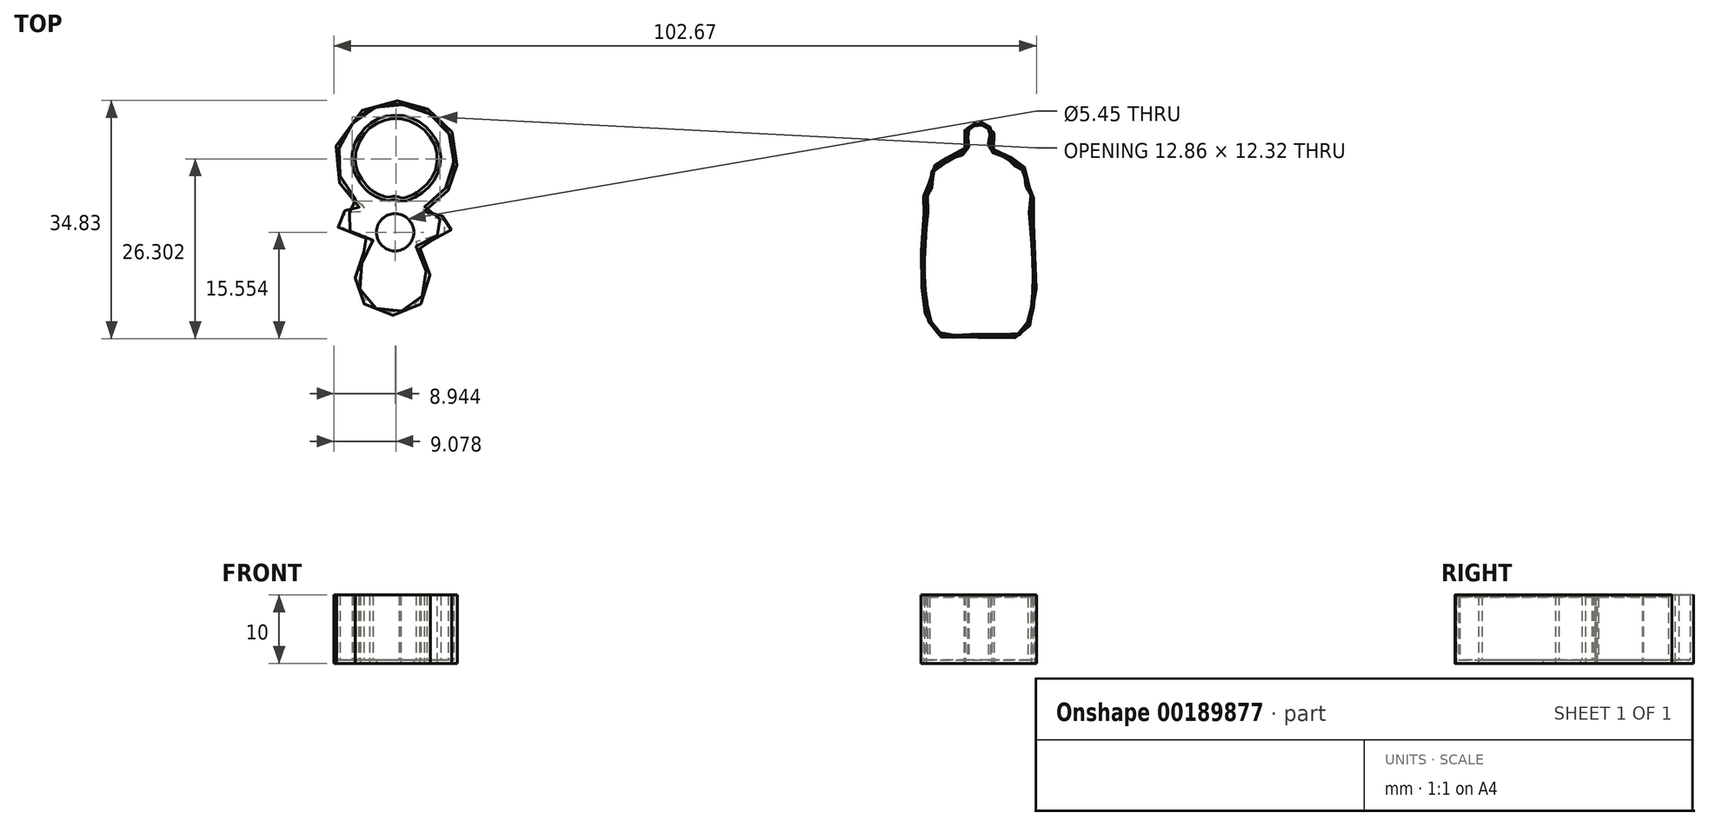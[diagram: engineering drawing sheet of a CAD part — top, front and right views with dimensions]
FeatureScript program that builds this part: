
annotation { "Feature Type Name" : "Feature", "Feature Type Description" : "" }
export const myFeature = defineFeature(function(context is Context, id is Id, definition is map)
    precondition{}
    {
        {
            var Q0;
            Q0=qCreatedBy(makeId("Top.planeOp"),FACE);
            var sketch = newSketch(context, id + "F0", { "sketchPlane" : qUnion([Q0])});
            skFitSpline(sketch, "E0", {"points": [v(-48.43, 29.19) * mm, v(-45.9, 31.2) * mm, v(-44.38, 33.3) * mm, v(-43.72, 35.4) * mm, v(-43.8, 39.13) * mm, v(-45.02, 41.74) * mm, v(-47.94, 44.21) * mm, v(-50.92, 45.2) * mm, v(-54.18, 45.32) * mm, v(-58.63, 43.06) * mm, v(-61.53, 37.77) * mm, v(-60.92, 33.6) * mm, v(-58.75, 30.52) * mm, v(-57.75, 29.7) * mm, v(-57.73, 29.65) * mm, v(-58.6, 29.62) * mm, v(-60.27, 29.17) * mm, v(-61.16, 28.22) * mm, v(-61.13, 27.06) * mm, v(-59.43, 25.82) * mm, v(-56.55, 25.26) * mm, v(-56.44, 25.26) * mm, v(-56.5, 24.8) * mm, v(-57.3, 23.15) * mm, v(-58.25, 21.18) * mm, v(-58.46, 18.34) * mm, v(-57.63, 16.15) * mm, v(-55.65, 14.53) * mm, v(-52.2, 14.04) * mm, v(-49.52, 15.11) * mm, v(-47.93, 17.32) * mm, v(-47.7, 20.56) * mm, v(-48.96, 23.46) * mm, v(-49.08, 23.89) * mm, v(-49.1, 24.68) * mm, v(-49, 24.74) * mm, v(-46.78, 25.09) * mm, v(-44.95, 25.77) * mm, v(-44.5, 26.48) * mm, v(-44.52, 27.45) * mm, v(-45.1, 28.21) * mm, v(-46.6, 28.74) * mm, v(-48.11, 29.1) * mm, v(-48.4, 29.14) * mm, v(-48.43, 29.19) * mm]});
            skFitSpline(sketch, "E1", {"points": [v(-51.83, 31.14) * mm, v(-50.03, 31.7) * mm, v(-49.62, 31.9) * mm, v(-47.4, 34) * mm, v(-46.84, 38.74) * mm, v(-50.67, 42.47) * mm, v(-55.22, 42.15) * mm, v(-58.4, 37.99) * mm], "startDerivative": vector(5.8, -4.1) * mm, "endDerivative": vector(-10.4, -36.58) * mm});
            skFitSpline(sketch, "E2", {"points": [v(-58.4, 37.99) * mm, v(-58.49, 37.04) * mm, v(-58.2, 35.19) * mm, v(-56.71, 32.82) * mm, v(-55.36, 31.86) * mm, v(-53.73, 31.29) * mm, v(-52.96, 31.42) * mm, v(-52.17, 31.34) * mm, v(-51.83, 31.14) * mm], "startDerivative": vector(-1.02, -8.1) * mm, "endDerivative": vector(4.18, -3.1) * mm});
            skSolve(sketch);
        }
        {
            var Q0;
            Q0 = qSketchRegion(id + "F0", true);
            extrude(context, id + "F1", {"entities" : qUnion([Q0]), "depth" : 10 * mm});
        }
        {
            var Q0;
            Q0=makeQuery(id+"F1.opExtrude","CAP_FACE",FACE,{"disambiguationData":[OSD([sQuery(id+"F0.wireOp",EDGE,"E0"),sQuery(id+"F0.wireOp",EDGE,"E1"),sQuery(id+"F0.wireOp",EDGE,"E2")])],"isStart":false});
            shell(context, id + "F2", {"entities" : qUnion([Q0]), "thickness" : .5 * mm});
        }
        {
            var Q0;
            Q0=makeQuery(id+"F1.opExtrude","CAP_FACE",FACE,{"disambiguationData":[OSD([sQuery(id+"F0.wireOp",EDGE,"E0"),sQuery(id+"F0.wireOp",EDGE,"E1"),sQuery(id+"F0.wireOp",EDGE,"E2")])],"isStart":true});
            var sketch = newSketch(context, id + "F3", { "sketchPlane" : qUnion([Q0])});
            skCircle(sketch, "E3", {"center": v(-52.69, -26.14) * mm, "radius": 2.73 * mm});
            skSolve(sketch);
        }
        {
            var Q0;
            Q0 = qSketchRegion(id + "F3", true);
            extrude(context, id + "F4", {"entities" : qUnion([Q0]), "operationType" : NewBodyOperationType.REMOVE, "oppositeDirection" : true, "depth" : 25 * mm});
        }
        {
            var Q0;
            Q0=qCreatedBy(makeId("Top.planeOp"),FACE);
            var sketch = newSketch(context, id + "F5", { "sketchPlane" : qUnion([Q0])});
            skFitSpline(sketch, "E4", {"points": [v(27.1, 10.85) * mm, v(32.38, 10.77) * mm, v(37.87, 10.72) * mm, v(39.08, 11.23) * mm, v(40.1, 12.62) * mm, v(41.04, 19.34) * mm, v(40.28, 31) * mm, v(40.29, 31.08) * mm, v(40.6, 31.13) * mm, v(40.74, 31.62) * mm, v(40.44, 32.07) * mm, v(40.07, 32.47) * mm, v(39.92, 33.77) * mm, v(39.15, 35.8) * mm, v(38.3, 36.15) * mm, v(37.9, 36.62) * mm, v(35.92, 37.88) * mm, v(34.92, 38.16) * mm, v(34.55, 38.8) * mm, v(34.7, 40.13) * mm, v(34.76, 41.12) * mm, v(33.82, 42.1) * mm, v(32.46, 42.28) * mm, v(30.92, 41.7) * mm, v(30.47, 40.2) * mm, v(30.63, 39) * mm, v(30.35, 38.11) * mm, v(28.7, 37.46) * mm, v(27.07, 36.33) * mm, v(26.96, 36.17) * mm, v(26.49, 36.08) * mm, v(25.65, 35.34) * mm, v(25.33, 33.66) * mm, v(25.16, 32.37) * mm, v(24.9, 32.14) * mm, v(24.56, 31.41) * mm, v(24.86, 31.08) * mm, v(24.76, 29.82) * mm, v(24.37, 25.45) * mm, v(24.18, 19.14) * mm, v(24.5, 16.32) * mm, v(25.1, 13.08) * mm, v(27.1, 10.85) * mm]});
            skSolve(sketch);
        }
        {
            var Q0;
            Q0 = qSketchRegion(id + "F5", true);
            extrude(context, id + "F6", {"entities" : qUnion([Q0]), "depth" : 10 * mm});
        }
        {
            var Q0;
            Q0=makeQuery(id+"F6.opExtrude","CAP_FACE",FACE,{"disambiguationData":[OSD([sQuery(id+"F5.wireOp",EDGE,"E4")])],"isStart":false});
            shell(context, id + "F7", {"entities" : qUnion([Q0]), "thickness" : .5 * mm});
        }
        {
            var Q0;
            {var subQ0=sQuery(id+"F5.wireOp",EDGE,"E4");Q0=makeQuery(id+"F7.opShell","OFFSET_EDGE",EDGE,{"disambiguationData":[OSD([subQ0]),TDD([makeQuery(id+"F6.opExtrude","CAP_EDGE",EDGE,{"disambiguationData":[OSD([subQ0])],"isStart":false})]),OD(1.0)]});}
            var Q1;
            {var subQ0=sQuery(id+"F5.wireOp",EDGE,"E4");Q1=makeQuery(id+"F7.opShell","OFFSET_EDGE",EDGE,{"disambiguationData":[OSD([subQ0]),TDD([makeQuery(id+"F6.opExtrude","CAP_EDGE",EDGE,{"disambiguationData":[OSD([subQ0])],"isStart":false})]),OD(0.0)]});}
            chamfer(context, id + "F8", {"entities" : qUnion([Q0, Q1]), "width" : .3 * mm, "tangentPropagation" : true});
        }
    });
